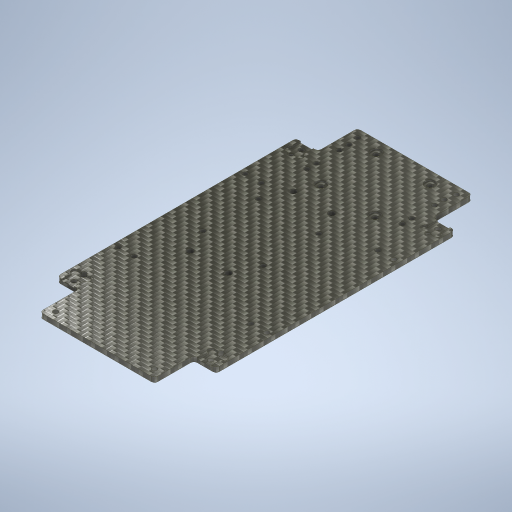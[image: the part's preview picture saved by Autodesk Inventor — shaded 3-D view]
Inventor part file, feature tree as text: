
AUTODESK INVENTOR PART (.ipt)
format: ipt  version: 2024.2 (Build 282272000, 272)  size: 553,472 bytes
history: native  units: mm
features: hole x3, extrude x2, sketch x1
ambient origin geometry x8: Origin, YZ Plane, XZ Plane, XY Plane, X Axis, Y Axis, Z Axis, Center Point
bodies: Solid1 (feature_tree)
feature tree (6):
  sketch  "Sketch1"  dims[d0=200.0mm d1=100.0mm d2=62.0mm d3=45.0mm d4=80.1mm d5=5.0mm d7=38.0mm d8=35.0mm d9=31.8mm d10=7.9mm d11=19.1mm d12=3.0mm d13=3.0mm d14=3.2mm d15=2.0mm d17=3.0mm d18=0.0mm d19=3.2mm d20=6.0mm d21=4.0mm d22=2.0mm d23=90.0deg d24=8.0mm d25=20.594885mm d26=2.0mm d27=87.0mm d28=24.0mm d29=1.5mm d30=4.0mm d31=6.0mm d32=4.0mm d33=2.0mm d34=90.0deg d35=8.0mm d36=20.594885mm d37=6.95mm d38=4.5mm d39=4.0mm d40=10.0mm d41=43.18mm d42=50.0mm d43=8.5mm d44=16.0mm d45=6.5mm d46=4.0mm d47=1.0mm d48=0.05mm d49=1.0mm d50=0.0mm d51=2.0mm d55=3.2mm d56=6.0mm d57=6.5mm d58=1.0mm d59=90.0deg d60=8.0mm d61=20.594885mm d62=6.0mm d63=5.0mm d64=20.32mm d65=10.0mm d67=80.0mm d66=0.25mm d68=14.3117mm d69=0.75mm d70=20.594885mm d71=0.0625mm d72=0.75mm d73=0.375mm]
  extrude  "Extrusion1"  Depth=100.0mm
  extrude  "Extrusion2"  Depth=10.0mm
  hole  "Phi3.2"  [1 undecoded]
  hole  "Phi4.0"  [1 undecoded]
  hole  "Phi6.5-3.2"  [1 undecoded]
note: 3 required parameter values undecoded (feature->parameter linkage not recoverable at this tier; creation-order binding heuristic only, values carry confidence <= 0.55)
